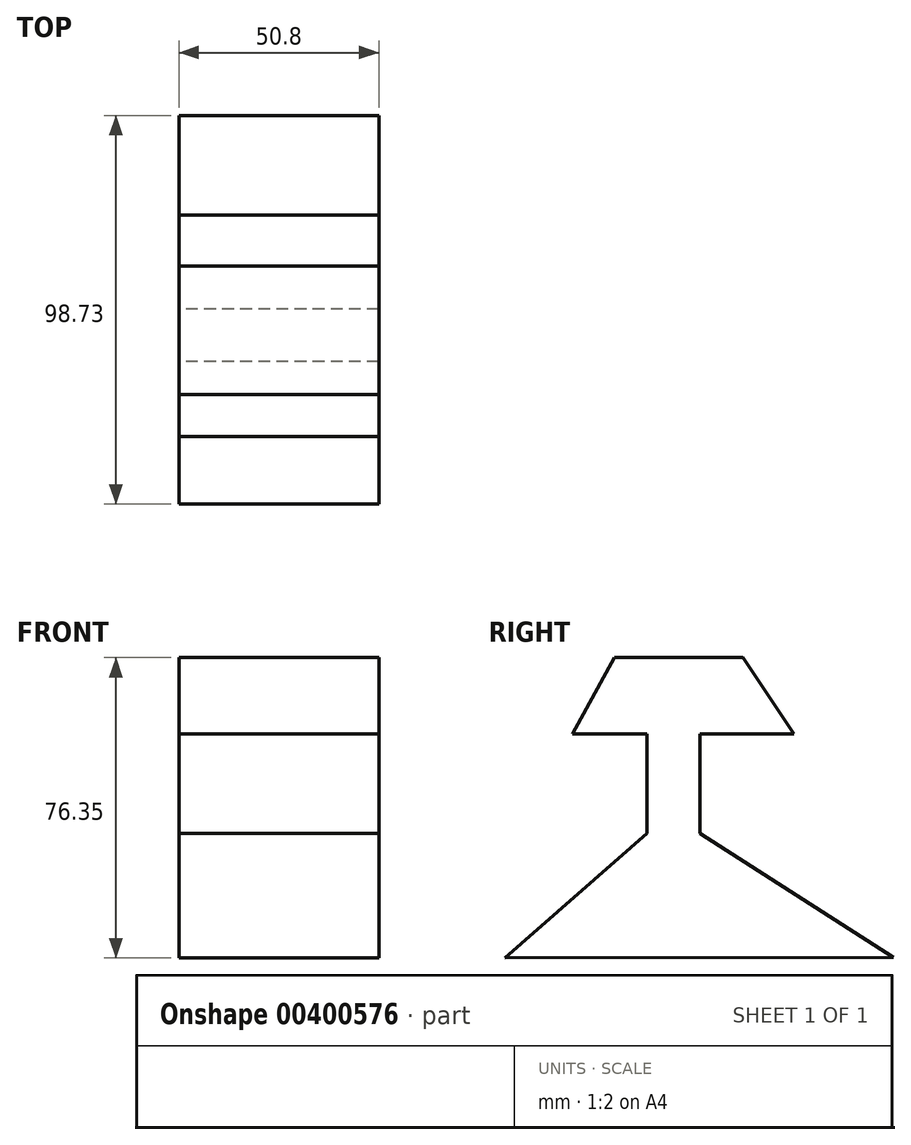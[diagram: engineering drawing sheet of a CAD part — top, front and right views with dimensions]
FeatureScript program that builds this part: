
annotation { "Feature Type Name" : "Feature", "Feature Type Description" : "" }
export const myFeature = defineFeature(function(context is Context, id is Id, definition is map)
    precondition{}
    {
        {
            var Q0;
            Q0=qCreatedBy(makeId("Right.planeOp"),FACE);
            var sketch = newSketch(context, id + "F0", { "sketchPlane" : qUnion([Q0])});
            skLineSegment(sketch, "E0", {"start": v(-15.48, 44.66) * mm, "end": v(-48.11, 44.66) * mm});
            skLineSegment(sketch, "E1", {"start": v(-48.11, 44.66) * mm, "end": v(-58.78, 25.2) * mm});
            skLineSegment(sketch, "E2", {"start": v(-58.78, 25.2) * mm, "end": v(-39.74, 25.2) * mm});
            skLineSegment(sketch, "E3", {"start": v(-15.48, 44.66) * mm, "end": v(-2.51, 25.2) * mm});
            skLineSegment(sketch, "E4", {"start": v(-2.51, 25.2) * mm, "end": v(-26.36, 25.2) * mm});
            skLineSegment(sketch, "E5", {"start": v(-26.36, 25.2) * mm, "end": v(-26.36, 0) * mm});
            skLineSegment(sketch, "E6", {"start": v(-39.74, 25.2) * mm, "end": v(-39.74, 0) * mm});
            skLineSegment(sketch, "E7", {"start": v(-26.36, 0) * mm, "end": v(22.8, -31.48) * mm});
            skLineSegment(sketch, "E8", {"start": v(-39.74, 0) * mm, "end": v(-75.93, -31.7) * mm});
            skLineSegment(sketch, "E9", {"start": v(22.8, -31.48) * mm, "end": v(-75.93, -31.7) * mm});
            skSolve(sketch);
        }
        {
            var Q0;
            Q0 = qSketchRegion(id + "F0", true);
            extrude(context, id + "F1", {"entities" : qUnion([Q0]), "depth" : 50.8 * mm});
        }
    });
